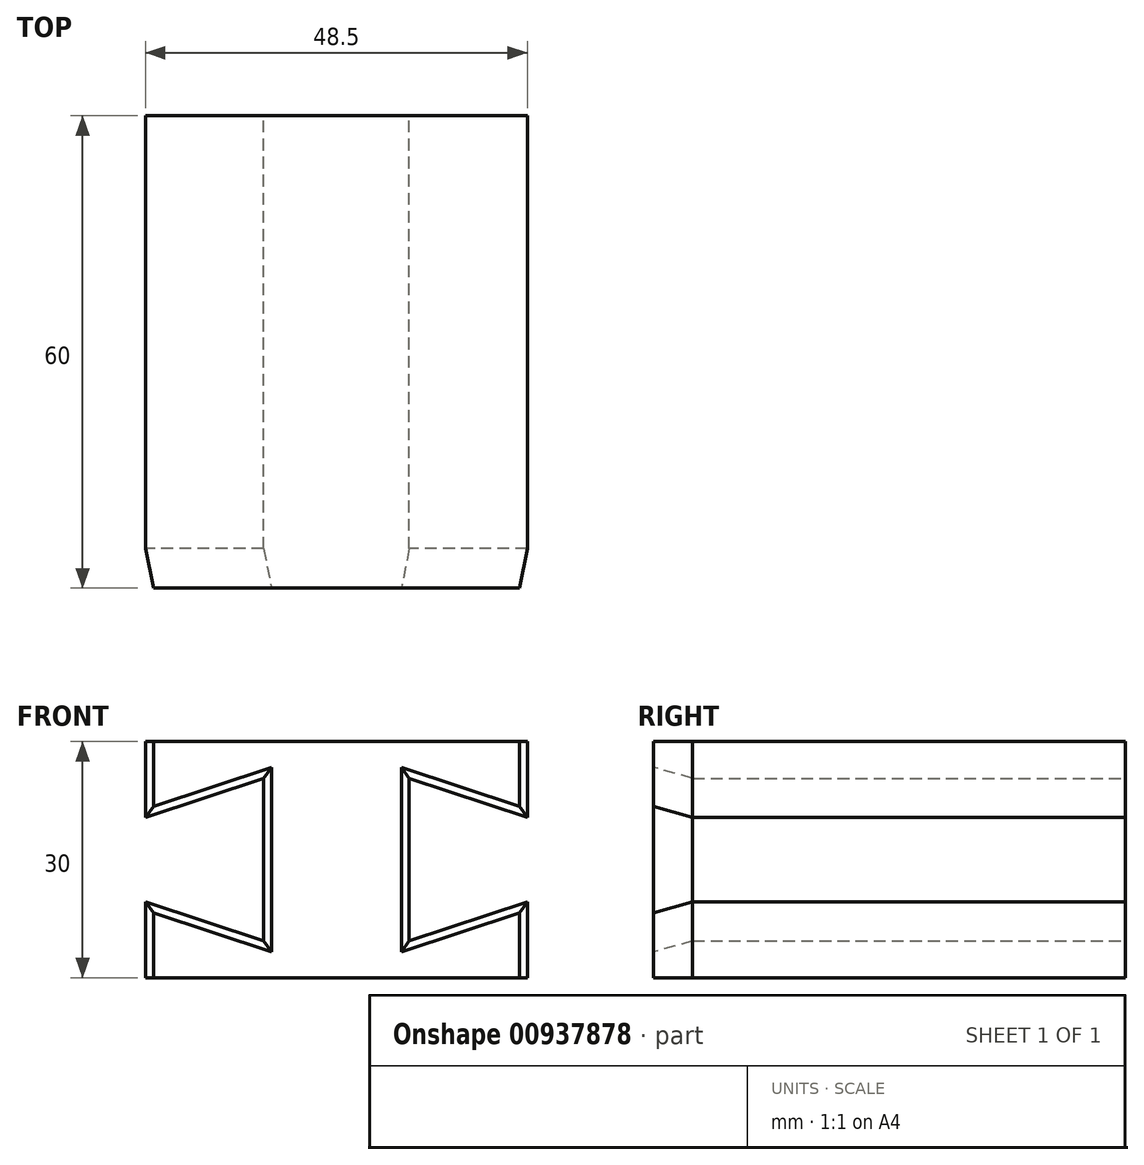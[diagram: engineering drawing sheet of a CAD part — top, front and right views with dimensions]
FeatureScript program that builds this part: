
annotation { "Feature Type Name" : "Feature", "Feature Type Description" : "" }
export const myFeature = defineFeature(function(context is Context, id is Id, definition is map)
    precondition{}
    {
        {
            var Q0;
            Q0=qCreatedBy(makeId("Front.planeOp"),FACE);
            var sketch = newSketch(context, id + "F0", { "sketchPlane" : qUnion([Q0])});
            skLineSegment(sketch, "E0", {"start": v(-24.5, 15) * mm, "end": v(-24.5, 5) * mm});
            skLineSegment(sketch, "E1", {"start": v(-24.5, 5) * mm, "end": v(-24.5, -5) * mm});
            skLineSegment(sketch, "E2", {"start": v(-24.5, -5) * mm, "end": v(-24.5, -15) * mm});
            skLineSegment(sketch, "E3", {"start": v(-24.5, 15) * mm, "end": v(-9.5, 15) * mm});
            skLineSegment(sketch, "E4", {"start": v(-9.5, 15) * mm, "end": v(0, 15) * mm});
            skLineSegment(sketch, "E5", {"start": v(-9.5, 15) * mm, "end": v(-9.5, 5) * mm});
            skLineSegment(sketch, "E6", {"start": v(-9.5, 5) * mm, "end": v(-9.5, -5) * mm});
            skLineSegment(sketch, "E7", {"start": v(-24.5, -15) * mm, "end": v(0, -15) * mm});
            skLineSegment(sketch, "E8", {"start": v(-9.5, -5) * mm, "end": v(-9.5, -15) * mm});
            skPoint(sketch, "E9", {"position": v(0, 15) * mm});
            skPoint(sketch, "E10", {"position": v(-9.5, 0) * mm});
            skLineSegment(sketch, "E11", {"start": v(-24.5, 5) * mm, "end": v(-9.5, 10) * mm});
            skLineSegment(sketch, "E12", {"start": v(-24.5, -5) * mm, "end": v(-9.5, -10) * mm});
            skLineSegment(sketch, "E13", {"start": v(-24.5, 10) * mm, "end": v(-9.25, 4.92) * mm});
            skLineSegment(sketch, "E14", {"start": v(-24.5, -10) * mm, "end": v(-9.5, -5) * mm});
            skLineSegment(sketch, "E15.0", {"start": v(-24.25, 5.35) * mm, "end": v(-9.25, 10.35) * mm});
            skLineSegment(sketch, "E15.1", {"start": v(-24.25, 15) * mm, "end": v(-24.25, 5.35) * mm});
            skLineSegment(sketch, "E16.0", {"start": v(-24.25, -5.35) * mm, "end": v(-24.25, -15) * mm});
            skLineSegment(sketch, "E16.1", {"start": v(-24.25, -5.35) * mm, "end": v(-9.25, -10.35) * mm});
            skLineSegment(sketch, "E17", {"start": v(0, 15) * mm, "end": v(0, -15) * mm});
            skLineSegment(sketch, "E18.2", {"start": v(-9.25, 15) * mm, "end": v(-9.25, -15) * mm});
            skSolve(sketch);
        }
        {
            var Q0;
            {var subQ0=sQuery(id+"F0.wireOp",EDGE,"E15.1");var subQ1=sQuery(id+"F0.wireOp",EDGE,"E13");var subQ2=makeQuery(id+"F0.imprint","INTERSECT",VERTEX,{"derivedFrom":[subQ1,subQ0]});Q0=makeQuery(id+"F0.imprint","IMPRINT",FACE,{"disambiguationData":[TD([[makeQuery(id+"F0.imprint","IMPRINT",EDGE,{"disambiguationData":[TD([[subQ2,-1.0]])],"derivedFrom":subQ1}),1.0]])]});}
            var Q1;
            {var subQ0=sQuery(id+"F0.wireOp",EDGE,"E15.1");var subQ1=sQuery(id+"F0.wireOp",EDGE,"E13");var subQ2=makeQuery(id+"F0.imprint","INTERSECT",VERTEX,{"derivedFrom":[subQ1,subQ0]});Q1=makeQuery(id+"F0.imprint","IMPRINT",FACE,{"disambiguationData":[TD([[makeQuery(id+"F0.imprint","IMPRINT",EDGE,{"disambiguationData":[TD([[subQ2,-1.0]])],"derivedFrom":subQ1}),-1.0]])]});}
            var Q2;
            {var subQ4=sQuery(id+"F0.wireOp",EDGE,"E17");Q2=makeQuery(id+"F0.imprint","IMPRINT",FACE,{"disambiguationData":[TD([[makeQuery(id+"F0.imprint","IMPRINT",EDGE,{"derivedFrom":subQ4}),-1.0]])]});}
            var Q3;
            {var subQ3=sQuery(id+"F0.wireOp",EDGE,"E18.2");var subQ5=sQuery(id+"F0.wireOp",EDGE,"E15.0");var subQ7=makeQuery(id+"F0.imprint","INTERSECT",VERTEX,{"derivedFrom":[subQ5,subQ3]});Q3=makeQuery(id+"F0.imprint","IMPRINT",FACE,{"disambiguationData":[TD([[makeQuery(id+"F0.imprint","IMPRINT",EDGE,{"disambiguationData":[TD([[subQ7,1.0]])],"derivedFrom":subQ5}),1.0]])]});}
            var Q4;
            {var subQ5=sQuery(id+"F0.wireOp",EDGE,"E8");var subQ6=sQuery(id+"F0.wireOp",EDGE,"E7");var subQ7=makeQuery(id+"F0.imprint","INTERSECT",VERTEX,{"derivedFrom":[subQ6,subQ5]});Q4=makeQuery(id+"F0.imprint","IMPRINT",FACE,{"disambiguationData":[TD([[makeQuery(id+"F0.imprint","IMPRINT",EDGE,{"disambiguationData":[TD([[subQ7,1.0]])],"derivedFrom":subQ6}),1.0]])]});}
            var Q5;
            {var subQ0=sQuery(id+"F0.wireOp",EDGE,"E16.0");var subQ1=sQuery(id+"F0.wireOp",EDGE,"E14");var subQ2=makeQuery(id+"F0.imprint","INTERSECT",VERTEX,{"derivedFrom":[subQ1,subQ0]});Q5=makeQuery(id+"F0.imprint","IMPRINT",FACE,{"disambiguationData":[TD([[makeQuery(id+"F0.imprint","IMPRINT",EDGE,{"disambiguationData":[TD([[subQ2,-1.0]])],"derivedFrom":subQ1}),1.0]])]});}
            var Q6;
            {var subQ0=sQuery(id+"F0.wireOp",EDGE,"E8");var subQ1=sQuery(id+"F0.wireOp",EDGE,"E7");var subQ2=makeQuery(id+"F0.imprint","INTERSECT",VERTEX,{"derivedFrom":[subQ1,subQ0]});Q6=makeQuery(id+"F0.imprint","IMPRINT",FACE,{"disambiguationData":[TD([[makeQuery(id+"F0.imprint","IMPRINT",EDGE,{"disambiguationData":[TD([[subQ2,-1.0]])],"derivedFrom":subQ1}),1.0]])]});}
            extrude(context, id + "F1", {"entities" : qUnion([Q0, Q1, Q2, Q3, Q4, Q5, Q6]), "depth" : 60 * mm, "offsetDistance" : 25 * mm});
        }
        {
            var Q0;
            Q0=makeQuery(id+"F1.opExtrude","SWEPT_BODY",BODY,{"disambiguationData":[OSD([sQuery(id+"F0.wireOp",EDGE,"E3"),sQuery(id+"F0.wireOp",EDGE,"E4"),sQuery(id+"F0.wireOp",EDGE,"E7"),sQuery(id+"F0.wireOp",EDGE,"E15.0"),sQuery(id+"F0.wireOp",EDGE,"E15.1"),sQuery(id+"F0.wireOp",EDGE,"E16.0"),sQuery(id+"F0.wireOp",EDGE,"E16.1"),sQuery(id+"F0.wireOp",EDGE,"E17"),sQuery(id+"F0.wireOp",EDGE,"E18.0"),sQuery(id+"F0.wireOp",EDGE,"E18.1"),sQuery(id+"F0.wireOp",EDGE,"E18.2")])]});
            var Q1;
            Q1=makeQuery(id+"F1.opExtrude","SWEPT_FACE",FACE,{"disambiguationData":[OSD([sQuery(id+"F0.wireOp",EDGE,"E17")])]});
            mirror(context, id + "F2", {"operationType" : NewBodyOperationType.ADD, "entities" : qUnion([Q0]), "mirrorPlane" : qUnion([Q1])});
        }
        {
            var Q0;
            Q0=makeQuery(id+"F1.opExtrude","CAP_EDGE",EDGE,{"disambiguationData":[OSD([sQuery(id+"F0.wireOp",EDGE,"E15.1")])],"isStart":false});
            var Q1;
            Q1=makeQuery(id+"F2.opPattern","COPY",EDGE,{"derivedFrom":makeQuery(id+"F1.opExtrude","CAP_EDGE",EDGE,{"disambiguationData":[OSD([sQuery(id+"F0.wireOp",EDGE,"E18.0"),sQuery(id+"F0.wireOp",EDGE,"E18.1"),sQuery(id+"F0.wireOp",EDGE,"E18.2")])],"isStart":false}),"instanceName":"1"});
            var Q2;
            Q2=makeQuery(id+"F2.opPattern","COPY",EDGE,{"derivedFrom":makeQuery(id+"F1.opExtrude","CAP_EDGE",EDGE,{"disambiguationData":[OSD([sQuery(id+"F0.wireOp",EDGE,"E15.0")])],"isStart":false}),"instanceName":"1"});
            var Q3;
            Q3=makeQuery(id+"F2.opPattern","COPY",EDGE,{"derivedFrom":makeQuery(id+"F1.opExtrude","CAP_EDGE",EDGE,{"disambiguationData":[OSD([sQuery(id+"F0.wireOp",EDGE,"E15.1")])],"isStart":false}),"instanceName":"1"});
            var Q4;
            Q4=makeQuery(id+"F1.opExtrude","CAP_EDGE",EDGE,{"disambiguationData":[OSD([sQuery(id+"F0.wireOp",EDGE,"E15.0")])],"isStart":false});
            var Q5;
            Q5=makeQuery(id+"F1.opExtrude","CAP_EDGE",EDGE,{"disambiguationData":[OSD([sQuery(id+"F0.wireOp",EDGE,"E18.0"),sQuery(id+"F0.wireOp",EDGE,"E18.1"),sQuery(id+"F0.wireOp",EDGE,"E18.2")])],"isStart":false});
            var Q6;
            Q6=makeQuery(id+"F1.opExtrude","CAP_EDGE",EDGE,{"disambiguationData":[OSD([sQuery(id+"F0.wireOp",EDGE,"E16.1")])],"isStart":false});
            var Q7;
            Q7=makeQuery(id+"F1.opExtrude","CAP_EDGE",EDGE,{"disambiguationData":[OSD([sQuery(id+"F0.wireOp",EDGE,"E16.0")])],"isStart":false});
            var Q8;
            Q8=makeQuery(id+"F2.opPattern","COPY",EDGE,{"derivedFrom":makeQuery(id+"F1.opExtrude","CAP_EDGE",EDGE,{"disambiguationData":[OSD([sQuery(id+"F0.wireOp",EDGE,"E16.1")])],"isStart":false}),"instanceName":"1"});
            var Q9;
            Q9=makeQuery(id+"F2.opPattern","COPY",EDGE,{"derivedFrom":makeQuery(id+"F1.opExtrude","CAP_EDGE",EDGE,{"disambiguationData":[OSD([sQuery(id+"F0.wireOp",EDGE,"E16.0")])],"isStart":false}),"instanceName":"1"});
            chamfer(context, id + "F3", {"entities" : qUnion([Q0, Q1, Q2, Q3, Q4, Q5, Q6, Q7, Q8, Q9]), "chamferType" : ChamferType.TWO_OFFSETS, "width1" : 1 * mm, "oppositeDirection" : false, "width2" : 5 * mm, "tangentPropagation" : true});
        }
    });
